# Revit family: Insulating-Panels_Isowall-base-103
name_source: partatom
category: Generic Models
units: mm (PartAtom-declared; Revit-internal decimal feet)

## family parameters
Always vertical = Yes
Can host rebar = No
Cut with Voids When Loaded = No
Host = Wall
Maintain Annotation Orientation = No
Part Type = Normal
Room Calculation Point = No
Round Connector Dimension = Use Diameter
Shared = No

## types (1)
- AIC-1.03
    Clip Material = Metal
    Clip Width = 0' - 1"
    Construction Details = https://www.arcat.com
    Default Elevation = 0' - 0"
    Description = 2" x 2" Angle Set In Buty Caulk And Fastened to Floor At 36" Centers. Concrete Anchors
    Isowall Panel Material = Wall Panel
    Keynote = 07 42 00
    Manufacturer = Advance Inulation Concepts, Inc.
    Model = AIC-1.03
    Panel Height = 0' - 10 13/32"
    Panel Thickness = 0' - 3 3/8"
    Product Documentation Link = https://www.arcat.com
    Specification = https://www.aicinsulate.com
    URL = https://www.aicinsulate.com

## geometry (parser evidence)
native form markers: Sweep x5
no freeform markers — native parametric forms only
